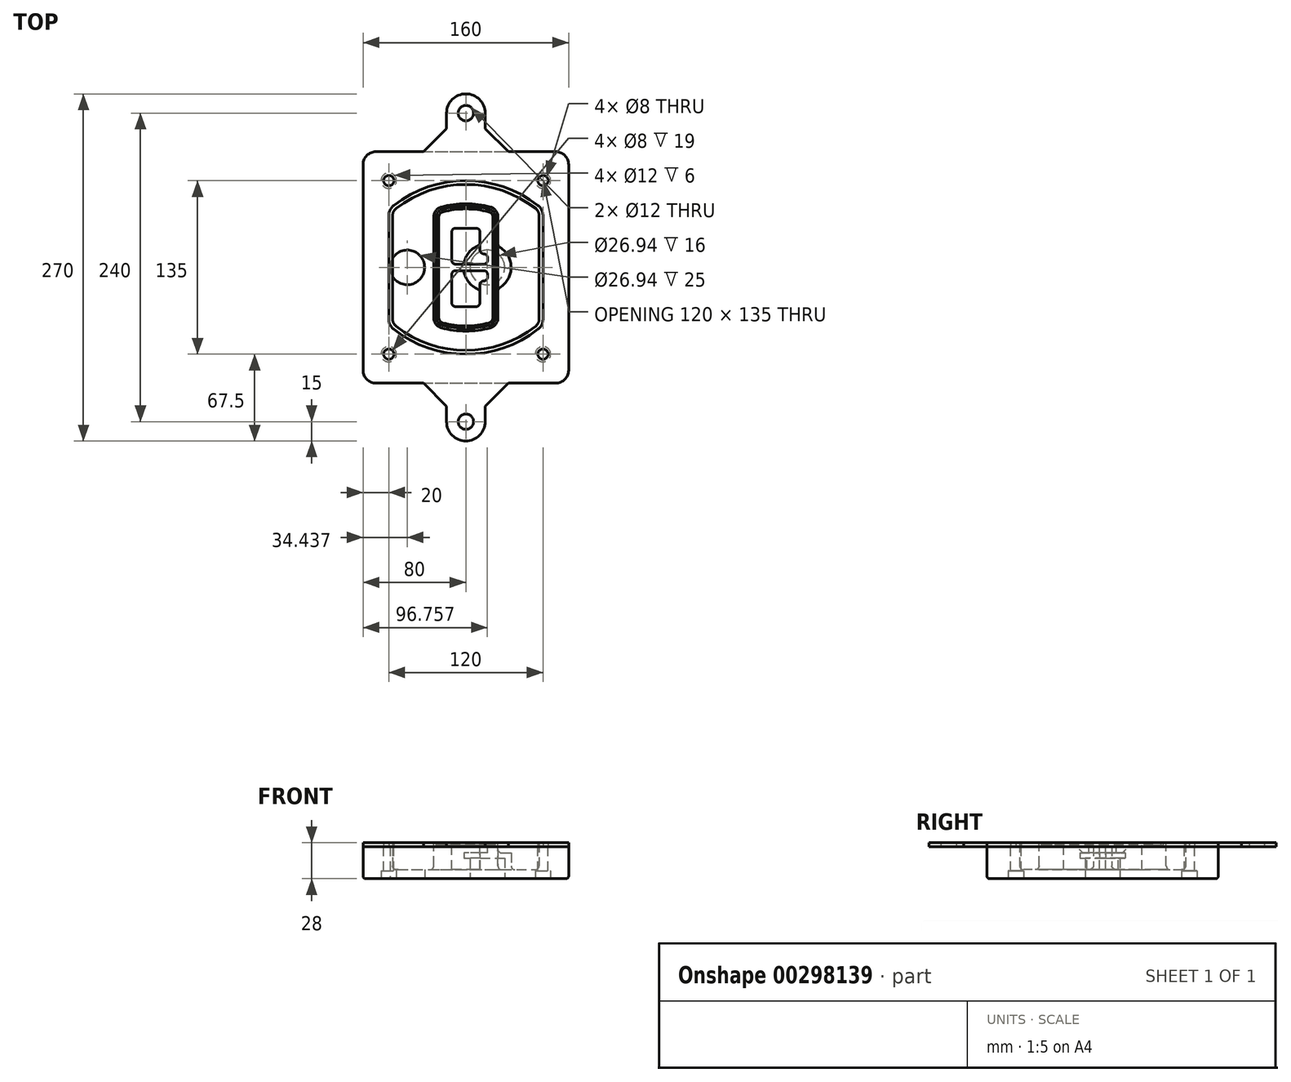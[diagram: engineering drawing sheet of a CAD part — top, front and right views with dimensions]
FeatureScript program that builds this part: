
annotation { "Feature Type Name" : "Feature", "Feature Type Description" : "" }
export const myFeature = defineFeature(function(context is Context, id is Id, definition is map)
    precondition{}
    {
        {
            var Q0;
            Q0=qCreatedBy(makeId("Top.planeOp"),FACE);
            var sketch = newSketch(context, id + "F0", { "sketchPlane" : qUnion([Q0])});
            skPoint(sketch, "E0.rect.middle", {"position": v(0, 0) * mm});
            skLineSegment(sketch, "E1.bottom", {"start": v(-70, -90) * mm, "end": v(70, -90) * mm});
            skLineSegment(sketch, "E1.top", {"start": v(-70, 90) * mm, "end": v(70, 90) * mm});
            skLineSegment(sketch, "E1.left", {"start": v(-80, -80) * mm, "end": v(-80, 80) * mm});
            skLineSegment(sketch, "E1.right", {"start": v(80, -80) * mm, "end": v(80, 80) * mm});
            skLineSegment(sketch, "E2", {"start": v(-80, 90) * mm, "end": v(80, -90) * mm, "construction": true});
            skLineSegment(sketch, "E3", {"start": v(80, 90) * mm, "end": v(-80, -90) * mm, "construction": true});
            skCircle(sketch, "E4", {"center": v(-60, 67.5) * mm, "radius": 4 * mm});
            skCircle(sketch, "E5", {"center": v(60, 67.5) * mm, "radius": 4 * mm});
            skCircle(sketch, "E6", {"center": v(60, -67.5) * mm, "radius": 4 * mm});
            skCircle(sketch, "E7", {"center": v(-60, -67.5) * mm, "radius": 4 * mm});
            skLineSegment(sketch, "E8", {"start": v(-60, 67.5) * mm, "end": v(60, 67.5) * mm, "construction": true});
            skLineSegment(sketch, "E9", {"start": v(60, 67.5) * mm, "end": v(60, -67.5) * mm, "construction": true});
            skLineSegment(sketch, "E10", {"start": v(60, -67.5) * mm, "end": v(-60, -67.5) * mm, "construction": true});
            skLineSegment(sketch, "E11", {"start": v(-60, -67.5) * mm, "end": v(-60, 67.5) * mm, "construction": true});
            skLineSegment(sketch, "E12", {"start": v(-60, 40.3) * mm, "end": v(-60, -40.3) * mm});
            skLineSegment(sketch, "E13", {"start": v(60, 40.3) * mm, "end": v(60, -40.3) * mm});
            skArc(sketch, "E14", {"start": v(56.15, 48.18) * mm, "mid": v(0, 67.5) * mm, "end": v(-56.15, 48.18) * mm});
            skArc(sketch, "E15", {"start": v(-56.15, -48.18) * mm, "mid": v(0, -67.5) * mm, "end": v(56.15, -48.18) * mm});
            skLineSegment(sketch, "E16", {"start": v(-60, 0) * mm, "end": v(60, 0) * mm, "construction": true});
            skPoint(sketch, "E17.visualSharp", {"position": v(-60, -45) * mm});
            skArc(sketch, "E17.filletArc", {"start": v(-60, -40.3) * mm, "mid": v(-58.99, -44.68) * mm, "end": v(-56.15, -48.18) * mm});
            skPoint(sketch, "E18.visualSharp", {"position": v(-60, 45) * mm});
            skArc(sketch, "E18.filletArc", {"start": v(-56.15, 48.18) * mm, "mid": v(-58.99, 44.68) * mm, "end": v(-60, 40.3) * mm});
            skPoint(sketch, "E19.visualSharp", {"position": v(60, 45) * mm});
            skArc(sketch, "E19.filletArc", {"start": v(60, 40.3) * mm, "mid": v(58.99, 44.68) * mm, "end": v(56.15, 48.18) * mm});
            skPoint(sketch, "E20.visualSharp", {"position": v(60, -45) * mm});
            skArc(sketch, "E20.filletArc", {"start": v(56.15, -48.18) * mm, "mid": v(58.99, -44.68) * mm, "end": v(60, -40.3) * mm});
            skPoint(sketch, "E21.visualSharp", {"position": v(-80, 90) * mm});
            skArc(sketch, "E21.filletArc", {"start": v(-70, 90) * mm, "mid": v(-77.07, 87.07) * mm, "end": v(-80, 80) * mm});
            skPoint(sketch, "E22.visualSharp", {"position": v(80, 90) * mm});
            skArc(sketch, "E22.filletArc", {"start": v(80, 80) * mm, "mid": v(77.07, 87.07) * mm, "end": v(70, 90) * mm});
            skPoint(sketch, "E23.visualSharp", {"position": v(80, -90) * mm});
            skArc(sketch, "E23.filletArc", {"start": v(70, -90) * mm, "mid": v(77.07, -87.07) * mm, "end": v(80, -80) * mm});
            skPoint(sketch, "E24.visualSharp", {"position": v(-80, -90) * mm});
            skArc(sketch, "E24.filletArc", {"start": v(-80, -80) * mm, "mid": v(-77.07, -87.07) * mm, "end": v(-70, -90) * mm});
            skArc(sketch, "E25.0", {"start": v(57, 40.3) * mm, "mid": v(56.3, 43.36) * mm, "end": v(54.3, 45.81) * mm});
            skLineSegment(sketch, "E25.1", {"start": v(57, 40.3) * mm, "end": v(57, -40.3) * mm});
            skArc(sketch, "E25.2", {"start": v(54.3, -45.81) * mm, "mid": v(56.3, -43.36) * mm, "end": v(57, -40.3) * mm});
            skArc(sketch, "E25.3", {"start": v(-54.3, -45.81) * mm, "mid": v(0, -64.5) * mm, "end": v(54.3, -45.81) * mm});
            skArc(sketch, "E25.4", {"start": v(-57, -40.3) * mm, "mid": v(-56.3, -43.36) * mm, "end": v(-54.3, -45.81) * mm});
            skArc(sketch, "E25.5", {"start": v(54.3, 45.81) * mm, "mid": v(0, 64.5) * mm, "end": v(-54.3, 45.81) * mm});
            skLineSegment(sketch, "E25.6", {"start": v(-57, 40.3) * mm, "end": v(-57, -40.3) * mm});
            skArc(sketch, "E25.7", {"start": v(-54.3, 45.81) * mm, "mid": v(-56.3, 43.36) * mm, "end": v(-57, 40.3) * mm});
            skArc(sketch, "E26.0", {"start": v(-58.62, 51.33) * mm, "mid": v(-62.58, 46.43) * mm, "end": v(-64, 40.3) * mm});
            skArc(sketch, "E26.1", {"start": v(58.62, 51.33) * mm, "mid": v(0, 71.5) * mm, "end": v(-58.62, 51.33) * mm});
            skArc(sketch, "E26.2", {"start": v(64, 40.3) * mm, "mid": v(62.58, 46.43) * mm, "end": v(58.62, 51.33) * mm});
            skLineSegment(sketch, "E26.3", {"start": v(64, 40.3) * mm, "end": v(64, -40.3) * mm});
            skArc(sketch, "E26.4", {"start": v(58.62, -51.33) * mm, "mid": v(62.58, -46.43) * mm, "end": v(64, -40.3) * mm});
            skLineSegment(sketch, "E26.5", {"start": v(-64, 40.3) * mm, "end": v(-64, -40.3) * mm});
            skArc(sketch, "E26.6", {"start": v(-58.62, -51.33) * mm, "mid": v(0, -71.5) * mm, "end": v(58.62, -51.33) * mm});
            skArc(sketch, "E26.7", {"start": v(-64, -40.3) * mm, "mid": v(-62.58, -46.43) * mm, "end": v(-58.62, -51.33) * mm});
            skSolve(sketch);
        }
        {
            var Q0;
            Q0=makeQuery(id+"F0.imprint","IMPRINT",FACE,{"disambiguationData":[TD([[makeQuery(id+"F0.imprint","IMPRINT",EDGE,{"derivedFrom":sQuery(id+"F0.wireOp",EDGE,"E1.bottom")}),1.0]])]});
            var Q1;
            Q1=makeQuery(id+"F0.imprint","IMPRINT",FACE,{"disambiguationData":[TD([[makeQuery(id+"F0.imprint","IMPRINT",EDGE,{"derivedFrom":sQuery(id+"F0.wireOp",EDGE,"E12")}),1.0]])]});
            var Q2;
            Q2=makeQuery(id+"F0.imprint","IMPRINT",FACE,{"disambiguationData":[TD([[makeQuery(id+"F0.imprint","IMPRINT",EDGE,{"derivedFrom":sQuery(id+"F0.wireOp",EDGE,"E25.0")}),1.0]])]});
            var Q3;
            Q3=makeQuery(id+"F0.imprint","IMPRINT",FACE,{"disambiguationData":[TD([[makeQuery(id+"F0.imprint","IMPRINT",EDGE,{"derivedFrom":sQuery(id+"F0.wireOp",EDGE,"E12")}),-1.0]])]});
            extrude(context, id + "F1", {"entities" : qUnion([Q0, Q1, Q2, Q3]), "oppositeDirection" : true, "depth" : 25 * mm});
        }
        {
            var Q0;
            Q0=makeQuery(id+"F0.imprint","IMPRINT",FACE,{"disambiguationData":[TD([[makeQuery(id+"F0.imprint","IMPRINT",EDGE,{"derivedFrom":sQuery(id+"F0.wireOp",EDGE,"E12")}),1.0]])]});
            extrude(context, id + "F2", {"entities" : qUnion([Q0]), "operationType" : NewBodyOperationType.ADD, "depth" : 3 * mm});
        }
        {
            var Q0;
            Q0=makeQuery(id+"F0.imprint","IMPRINT",FACE,{"disambiguationData":[TD([[makeQuery(id+"F0.imprint","IMPRINT",EDGE,{"derivedFrom":sQuery(id+"F0.wireOp",EDGE,"E25.0")}),1.0]])]});
            extrude(context, id + "F3", {"entities" : qUnion([Q0]), "operationType" : NewBodyOperationType.REMOVE, "oppositeDirection" : true, "depth" : 18 * mm});
        }
        {
            var Q0;
            Q0=makeQuery(id+"F2.opExtrude","CAP_FACE",FACE,{"disambiguationData":[OSD([sQuery(id+"F0.wireOp",EDGE,"E12"),sQuery(id+"F0.wireOp",EDGE,"E13"),sQuery(id+"F0.wireOp",EDGE,"E14"),sQuery(id+"F0.wireOp",EDGE,"E15"),sQuery(id+"F0.wireOp",EDGE,"E17.filletArc"),sQuery(id+"F0.wireOp",EDGE,"E18.filletArc"),sQuery(id+"F0.wireOp",EDGE,"E19.filletArc"),sQuery(id+"F0.wireOp",EDGE,"E20.filletArc"),sQuery(id+"F0.wireOp",EDGE,"E25.0"),sQuery(id+"F0.wireOp",EDGE,"E25.1"),sQuery(id+"F0.wireOp",EDGE,"E25.2"),sQuery(id+"F0.wireOp",EDGE,"E25.3"),sQuery(id+"F0.wireOp",EDGE,"E25.4"),sQuery(id+"F0.wireOp",EDGE,"E25.5"),sQuery(id+"F0.wireOp",EDGE,"E25.6"),sQuery(id+"F0.wireOp",EDGE,"E25.7")])],"isStart":false});
            var sketch = newSketch(context, id + "F4", { "sketchPlane" : qUnion([Q0])});
            skArc(sketch, "E27.0", {"start": v(-19.08, -46.97) * mm, "mid": v(0, -49.5) * mm, "end": v(19.08, -46.97) * mm});
            skArc(sketch, "E28.0", {"start": v(19.08, 46.97) * mm, "mid": v(0, 49.5) * mm, "end": v(-19.08, 46.97) * mm});
            skLineSegment(sketch, "E29", {"start": v(-25, 39.25) * mm, "end": v(-25, -39.25) * mm});
            skLineSegment(sketch, "E30", {"start": v(25, 39.25) * mm, "end": v(25, -39.25) * mm});
            skLineSegment(sketch, "E31", {"start": v(-25, 45.1) * mm, "end": v(25, 45.1) * mm, "construction": true});
            skLineSegment(sketch, "E32", {"start": v(-25, -45.1) * mm, "end": v(25, -45.1) * mm, "construction": true});
            skPoint(sketch, "E33.visualSharp", {"position": v(-25, 45.1) * mm});
            skArc(sketch, "E33.filletArc", {"start": v(-19.08, 46.97) * mm, "mid": v(-23.35, 44.11) * mm, "end": v(-25, 39.25) * mm});
            skPoint(sketch, "E34.visualSharp", {"position": v(25, 45.1) * mm});
            skArc(sketch, "E34.filletArc", {"start": v(25, 39.25) * mm, "mid": v(23.35, 44.11) * mm, "end": v(19.08, 46.97) * mm});
            skPoint(sketch, "E35.visualSharp", {"position": v(25, -45.1) * mm});
            skArc(sketch, "E35.filletArc", {"start": v(19.08, -46.97) * mm, "mid": v(23.35, -44.11) * mm, "end": v(25, -39.25) * mm});
            skPoint(sketch, "E36.visualSharp", {"position": v(-25, -45.1) * mm});
            skArc(sketch, "E36.filletArc", {"start": v(-25, -39.25) * mm, "mid": v(-23.35, -44.11) * mm, "end": v(-19.08, -46.97) * mm});
            skArc(sketch, "E37.0", {"start": v(54.3, 45.81) * mm, "mid": v(0, 64.5) * mm, "end": v(-54.3, 45.81) * mm});
            skArc(sketch, "E37.1", {"start": v(-54.3, 45.81) * mm, "mid": v(-56.3, 43.36) * mm, "end": v(-57, 40.3) * mm});
            skLineSegment(sketch, "E37.2", {"start": v(-57, 40.3) * mm, "end": v(-57, -40.3) * mm});
            skArc(sketch, "E37.3", {"start": v(-57, -40.3) * mm, "mid": v(-56.3, -43.36) * mm, "end": v(-54.3, -45.81) * mm});
            skArc(sketch, "E37.4", {"start": v(-54.3, -45.81) * mm, "mid": v(0, -64.5) * mm, "end": v(54.3, -45.81) * mm});
            skArc(sketch, "E37.5", {"start": v(54.3, -45.81) * mm, "mid": v(56.3, -43.36) * mm, "end": v(57, -40.3) * mm});
            skLineSegment(sketch, "E37.6", {"start": v(57, 40.3) * mm, "end": v(57, -40.3) * mm});
            skArc(sketch, "E37.7", {"start": v(57, 40.3) * mm, "mid": v(56.3, 43.36) * mm, "end": v(54.3, 45.81) * mm});
            skLineSegment(sketch, "E38.0", {"start": v(23, 39.25) * mm, "end": v(23, -39.25) * mm});
            skArc(sketch, "E38.1", {"start": v(18.56, -45.04) * mm, "mid": v(21.76, -42.9) * mm, "end": v(23, -39.25) * mm});
            skArc(sketch, "E38.2", {"start": v(-18.56, -45.04) * mm, "mid": v(0, -47.5) * mm, "end": v(18.56, -45.04) * mm});
            skArc(sketch, "E38.3", {"start": v(-23, -39.25) * mm, "mid": v(-21.76, -42.9) * mm, "end": v(-18.56, -45.04) * mm});
            skLineSegment(sketch, "E38.4", {"start": v(-23, 39.25) * mm, "end": v(-23, -39.25) * mm});
            skArc(sketch, "E38.5", {"start": v(23, 39.25) * mm, "mid": v(21.76, 42.9) * mm, "end": v(18.56, 45.04) * mm});
            skArc(sketch, "E38.6", {"start": v(-18.56, 45.04) * mm, "mid": v(-21.76, 42.9) * mm, "end": v(-23, 39.25) * mm});
            skArc(sketch, "E38.7", {"start": v(18.56, 45.04) * mm, "mid": v(0, 47.5) * mm, "end": v(-18.56, 45.04) * mm});
            skArc(sketch, "E39.0", {"start": v(21, 39.25) * mm, "mid": v(20.18, 41.68) * mm, "end": v(18.04, 43.1) * mm});
            skLineSegment(sketch, "E39.1", {"start": v(21, 39.25) * mm, "end": v(21, -39.25) * mm});
            skArc(sketch, "E39.2", {"start": v(18.04, -43.1) * mm, "mid": v(20.18, -41.68) * mm, "end": v(21, -39.25) * mm});
            skArc(sketch, "E39.3", {"start": v(-18.04, -43.1) * mm, "mid": v(0, -45.5) * mm, "end": v(18.04, -43.1) * mm});
            skArc(sketch, "E39.4", {"start": v(-21, -39.25) * mm, "mid": v(-20.18, -41.68) * mm, "end": v(-18.04, -43.1) * mm});
            skArc(sketch, "E39.5", {"start": v(18.04, 43.1) * mm, "mid": v(0, 45.5) * mm, "end": v(-18.04, 43.1) * mm});
            skLineSegment(sketch, "E39.6", {"start": v(-21, 39.25) * mm, "end": v(-21, -39.25) * mm});
            skArc(sketch, "E39.7", {"start": v(-18.04, 43.1) * mm, "mid": v(-20.18, 41.68) * mm, "end": v(-21, 39.25) * mm});
            skLineSegment(sketch, "E40", {"start": v(-25, 0) * mm, "end": v(25, 0) * mm, "construction": true});
            skLineSegment(sketch, "E41", {"start": v(-11, 5.5) * mm, "end": v(-11, 27.5) * mm});
            skLineSegment(sketch, "E42", {"start": v(-8, 30.5) * mm, "end": v(8, 30.5) * mm});
            skLineSegment(sketch, "E43", {"start": v(11, 27.5) * mm, "end": v(11, 13.5) * mm});
            skLineSegment(sketch, "E44", {"start": v(14, 10.5) * mm, "end": v(14, 10.5) * mm});
            skLineSegment(sketch, "E45", {"start": v(17, 7.5) * mm, "end": v(17, 5.5) * mm});
            skLineSegment(sketch, "E46", {"start": v(14, 2.5) * mm, "end": v(-8, 2.5) * mm});
            skPoint(sketch, "E47.visualSharp", {"position": v(-11, 30.5) * mm});
            skArc(sketch, "E47.filletArc", {"start": v(-8, 30.5) * mm, "mid": v(-10.12, 29.62) * mm, "end": v(-11, 27.5) * mm});
            skPoint(sketch, "E48.visualSharp", {"position": v(11, 30.5) * mm});
            skArc(sketch, "E48.filletArc", {"start": v(11, 27.5) * mm, "mid": v(10.12, 29.62) * mm, "end": v(8, 30.5) * mm});
            skPoint(sketch, "E49.visualSharp", {"position": v(11, 10.5) * mm});
            skArc(sketch, "E49.filletArc", {"start": v(11, 13.5) * mm, "mid": v(11.88, 11.38) * mm, "end": v(14, 10.5) * mm});
            skPoint(sketch, "E50.visualSharp", {"position": v(17, 10.5) * mm});
            skArc(sketch, "E50.filletArc", {"start": v(17, 7.5) * mm, "mid": v(16.12, 9.62) * mm, "end": v(14, 10.5) * mm});
            skPoint(sketch, "E51.visualSharp", {"position": v(17, 2.5) * mm});
            skArc(sketch, "E51.filletArc", {"start": v(14, 2.5) * mm, "mid": v(16.12, 3.38) * mm, "end": v(17, 5.5) * mm});
            skPoint(sketch, "E52.visualSharp", {"position": v(-11, 2.5) * mm});
            skArc(sketch, "E52.filletArc", {"start": v(-11, 5.5) * mm, "mid": v(-10.12, 3.38) * mm, "end": v(-8, 2.5) * mm});
            skLineSegment(sketch, "E53.0.MirrorCS", {"start": v(14, -2.5) * mm, "end": v(-8, -2.5) * mm});
            skArc(sketch, "E54.0.MirrorCS", {"start": v(-11, -5.5) * mm, "mid": v(-10.12, -3.38) * mm, "end": v(-8, -2.5) * mm});
            skLineSegment(sketch, "E55.0.MirrorCS", {"start": v(-11, -5.5) * mm, "end": v(-11, -27.5) * mm});
            skArc(sketch, "E56.0.MirrorCS", {"start": v(-8, -30.5) * mm, "mid": v(-10.12, -29.62) * mm, "end": v(-11, -27.5) * mm});
            skLineSegment(sketch, "E57.0.MirrorCS", {"start": v(-8, -30.5) * mm, "end": v(8, -30.5) * mm});
            skArc(sketch, "E58.0.MirrorCS", {"start": v(11, -27.5) * mm, "mid": v(10.12, -29.62) * mm, "end": v(8, -30.5) * mm});
            skLineSegment(sketch, "E59.0.MirrorCS", {"start": v(11, -27.5) * mm, "end": v(11, -13.5) * mm});
            skArc(sketch, "E60.0.MirrorCS", {"start": v(11, -13.5) * mm, "mid": v(11.88, -11.38) * mm, "end": v(14, -10.5) * mm});
            skArc(sketch, "E61.0.MirrorCS", {"start": v(17, -7.5) * mm, "mid": v(16.12, -9.62) * mm, "end": v(14, -10.5) * mm});
            skLineSegment(sketch, "E62.0.MirrorCS", {"start": v(17, -7.5) * mm, "end": v(17, -5.5) * mm});
            skArc(sketch, "E63.0.MirrorCS", {"start": v(14, -2.5) * mm, "mid": v(16.12, -3.38) * mm, "end": v(17, -5.5) * mm});
            skSolve(sketch);
        }
        {
            var Q0;
            Q0=makeQuery(id+"F4.imprint","IMPRINT",FACE,{"disambiguationData":[TD([[makeQuery(id+"F4.imprint","IMPRINT",EDGE,{"derivedFrom":sQuery(id+"F4.wireOp",EDGE,"E27.0")}),1.0]])]});
            var Q1;
            Q1=makeQuery(id+"F4.imprint","IMPRINT",FACE,{"disambiguationData":[TD([[makeQuery(id+"F4.imprint","IMPRINT",EDGE,{"derivedFrom":sQuery(id+"F4.wireOp",EDGE,"E38.0")}),-1.0]])]});
            var Q2;
            Q2=makeQuery(id+"F4.imprint","IMPRINT",FACE,{"disambiguationData":[TD([[makeQuery(id+"F4.imprint","IMPRINT",EDGE,{"derivedFrom":sQuery(id+"F4.wireOp",EDGE,"E39.0")}),1.0]])]});
            extrude(context, id + "F5", {"entities" : qUnion([Q0, Q1, Q2]), "operationType" : NewBodyOperationType.ADD, "endBound" : BoundingType.UP_TO_NEXT, "oppositeDirection" : true, "depth" : 25 * mm});
        }
        {
            var Q0;
            Q0=makeQuery(id+"F4.imprint","IMPRINT",FACE,{"disambiguationData":[TD([[makeQuery(id+"F4.imprint","IMPRINT",EDGE,{"derivedFrom":sQuery(id+"F4.wireOp",EDGE,"E38.0")}),-1.0]])]});
            extrude(context, id + "F6", {"entities" : qUnion([Q0]), "operationType" : NewBodyOperationType.REMOVE, "oppositeDirection" : true, "depth" : 2 * mm});
        }
        {
            var Q0;
            Q0=makeQuery(id+"F1.opExtrude","CAP_FACE",FACE,{"disambiguationData":[OSD([sQuery(id+"F0.wireOp",EDGE,"E1.bottom"),sQuery(id+"F0.wireOp",EDGE,"E1.top"),sQuery(id+"F0.wireOp",EDGE,"E1.left"),sQuery(id+"F0.wireOp",EDGE,"E1.right"),sQuery(id+"F0.wireOp",EDGE,"E4"),sQuery(id+"F0.wireOp",EDGE,"E5"),sQuery(id+"F0.wireOp",EDGE,"E6"),sQuery(id+"F0.wireOp",EDGE,"E7"),sQuery(id+"F0.wireOp",EDGE,"E21.filletArc"),sQuery(id+"F0.wireOp",EDGE,"E22.filletArc"),sQuery(id+"F0.wireOp",EDGE,"E23.filletArc"),sQuery(id+"F0.wireOp",EDGE,"E24.filletArc")])],"isStart":false});
            var sketch = newSketch(context, id + "F7", { "sketchPlane" : qUnion([Q0])});
            skCircle(sketch, "E64", {"center": v(16.76, 0) * mm, "radius": 13.47 * mm});
            skCircle(sketch, "E65", {"center": v(-45.56, 0) * mm, "radius": 13.47 * mm});
            skLineSegment(sketch, "E66", {"start": v(80, 0) * mm, "end": v(-80, 0) * mm});
            skCircle(sketch, "E67", {"center": v(16.76, 0) * mm, "radius": 18.47 * mm});
            skCircle(sketch, "E68", {"center": v(60, -67.5) * mm, "radius": 6 * mm});
            skCircle(sketch, "E69", {"center": v(-60, -67.5) * mm, "radius": 6 * mm});
            skCircle(sketch, "E70", {"center": v(-60, 67.5) * mm, "radius": 6 * mm});
            skCircle(sketch, "E71", {"center": v(60, 67.5) * mm, "radius": 6 * mm});
            skSolve(sketch);
        }
        {
            var Q0;
            {var subQ1=sQuery(id+"F7.wireOp",EDGE,"E66");var subQ4=sQuery(id+"F7.wireOp",EDGE,"E64");var subQ6=makeQuery(id+"F7.imprint","INTERSECT",VERTEX,{"disambiguationData":[OD(0.0)],"derivedFrom":[subQ4,subQ1]});Q0=makeQuery(id+"F7.imprint","IMPRINT",FACE,{"disambiguationData":[TD([[makeQuery(id+"F7.imprint","IMPRINT",EDGE,{"disambiguationData":[TD([[subQ6,-1.0]])],"derivedFrom":subQ4}),-1.0]])]});}
            var Q1;
            {var subQ0=sQuery(id+"F7.wireOp",EDGE,"E66");var subQ1=sQuery(id+"F7.wireOp",EDGE,"E64");var subQ3=makeQuery(id+"F7.imprint","INTERSECT",VERTEX,{"disambiguationData":[OD(0.0)],"derivedFrom":[subQ1,subQ0]});Q1=makeQuery(id+"F7.imprint","IMPRINT",FACE,{"disambiguationData":[TD([[makeQuery(id+"F7.imprint","IMPRINT",EDGE,{"disambiguationData":[TD([[subQ3,-1.0]])],"derivedFrom":subQ1}),1.0]])]});}
            var Q2;
            {var subQ0=sQuery(id+"F7.wireOp",EDGE,"E66");var subQ1=sQuery(id+"F7.wireOp",EDGE,"E64");var subQ3=makeQuery(id+"F7.imprint","INTERSECT",VERTEX,{"disambiguationData":[OD(0.0)],"derivedFrom":[subQ1,subQ0]});Q2=makeQuery(id+"F7.imprint","IMPRINT",FACE,{"disambiguationData":[TD([[makeQuery(id+"F7.imprint","IMPRINT",EDGE,{"disambiguationData":[TD([[subQ3,1.0]])],"derivedFrom":subQ1}),1.0]])]});}
            var Q3;
            {var subQ1=sQuery(id+"F7.wireOp",EDGE,"E66");var subQ4=sQuery(id+"F7.wireOp",EDGE,"E64");var subQ6=makeQuery(id+"F7.imprint","INTERSECT",VERTEX,{"disambiguationData":[OD(0.0)],"derivedFrom":[subQ4,subQ1]});Q3=makeQuery(id+"F7.imprint","IMPRINT",FACE,{"disambiguationData":[TD([[makeQuery(id+"F7.imprint","IMPRINT",EDGE,{"disambiguationData":[TD([[subQ6,1.0]])],"derivedFrom":subQ4}),-1.0]])]});}
            extrude(context, id + "F8", {"entities" : qUnion([Q0, Q1, Q2, Q3]), "operationType" : NewBodyOperationType.ADD, "oppositeDirection" : true, "depth" : 20 * mm});
        }
        {
            var Q0;
            {var subQ0=sQuery(id+"F7.wireOp",EDGE,"E66");var subQ1=sQuery(id+"F7.wireOp",EDGE,"E64");var subQ3=makeQuery(id+"F7.imprint","INTERSECT",VERTEX,{"disambiguationData":[OD(0.0)],"derivedFrom":[subQ1,subQ0]});Q0=makeQuery(id+"F7.imprint","IMPRINT",FACE,{"disambiguationData":[TD([[makeQuery(id+"F7.imprint","IMPRINT",EDGE,{"disambiguationData":[TD([[subQ3,-1.0]])],"derivedFrom":subQ1}),1.0]])]});}
            var Q1;
            {var subQ0=sQuery(id+"F7.wireOp",EDGE,"E66");var subQ1=sQuery(id+"F7.wireOp",EDGE,"E64");var subQ3=makeQuery(id+"F7.imprint","INTERSECT",VERTEX,{"disambiguationData":[OD(0.0)],"derivedFrom":[subQ1,subQ0]});Q1=makeQuery(id+"F7.imprint","IMPRINT",FACE,{"disambiguationData":[TD([[makeQuery(id+"F7.imprint","IMPRINT",EDGE,{"disambiguationData":[TD([[subQ3,1.0]])],"derivedFrom":subQ1}),1.0]])]});}
            extrude(context, id + "F9", {"entities" : qUnion([Q0, Q1]), "operationType" : NewBodyOperationType.REMOVE, "oppositeDirection" : true, "depth" : 16 * mm});
        }
        {
            var Q0;
            {var subQ0=sQuery(id+"F7.wireOp",EDGE,"E66");var subQ1=sQuery(id+"F7.wireOp",EDGE,"E65");var subQ3=makeQuery(id+"F7.imprint","INTERSECT",VERTEX,{"disambiguationData":[OD(0.0)],"derivedFrom":[subQ1,subQ0]});Q0=makeQuery(id+"F7.imprint","IMPRINT",FACE,{"disambiguationData":[TD([[makeQuery(id+"F7.imprint","IMPRINT",EDGE,{"disambiguationData":[TD([[subQ3,-1.0]])],"derivedFrom":subQ1}),1.0]])]});}
            var Q1;
            {var subQ0=sQuery(id+"F7.wireOp",EDGE,"E66");var subQ1=sQuery(id+"F7.wireOp",EDGE,"E65");var subQ3=makeQuery(id+"F7.imprint","INTERSECT",VERTEX,{"disambiguationData":[OD(0.0)],"derivedFrom":[subQ1,subQ0]});Q1=makeQuery(id+"F7.imprint","IMPRINT",FACE,{"disambiguationData":[TD([[makeQuery(id+"F7.imprint","IMPRINT",EDGE,{"disambiguationData":[TD([[subQ3,1.0]])],"derivedFrom":subQ1}),1.0]])]});}
            extrude(context, id + "F10", {"entities" : qUnion([Q0, Q1]), "operationType" : NewBodyOperationType.REMOVE, "oppositeDirection" : true, "depth" : 25 * mm});
        }
        {
            var Q0;
            Q0=makeQuery(id+"F7.imprint","IMPRINT",FACE,{"disambiguationData":[TD([[makeQuery(id+"F7.imprint","IMPRINT",EDGE,{"derivedFrom":sQuery(id+"F7.wireOp",EDGE,"E68")}),1.0]])]});
            var Q1;
            Q1=makeQuery(id+"F7.imprint","IMPRINT",FACE,{"disambiguationData":[TD([[makeQuery(id+"F7.imprint","IMPRINT",EDGE,{"derivedFrom":makeQuery(id+"F1.opExtrude","CAP_EDGE",EDGE,{"disambiguationData":[OSD([sQuery(id+"F0.wireOp",EDGE,"E5")])],"isStart":false})}),-1.0]])]});
            var Q2;
            Q2=makeQuery(id+"F7.imprint","IMPRINT",FACE,{"disambiguationData":[TD([[makeQuery(id+"F7.imprint","IMPRINT",EDGE,{"derivedFrom":sQuery(id+"F7.wireOp",EDGE,"E69")}),1.0]])]});
            var Q3;
            Q3=makeQuery(id+"F7.imprint","IMPRINT",FACE,{"disambiguationData":[TD([[makeQuery(id+"F7.imprint","IMPRINT",EDGE,{"derivedFrom":makeQuery(id+"F1.opExtrude","CAP_EDGE",EDGE,{"disambiguationData":[OSD([sQuery(id+"F0.wireOp",EDGE,"E4")])],"isStart":false})}),-1.0]])]});
            var Q4;
            Q4=makeQuery(id+"F7.imprint","IMPRINT",FACE,{"disambiguationData":[TD([[makeQuery(id+"F7.imprint","IMPRINT",EDGE,{"derivedFrom":sQuery(id+"F7.wireOp",EDGE,"E70")}),1.0]])]});
            var Q5;
            Q5=makeQuery(id+"F7.imprint","IMPRINT",FACE,{"disambiguationData":[TD([[makeQuery(id+"F7.imprint","IMPRINT",EDGE,{"derivedFrom":makeQuery(id+"F1.opExtrude","CAP_EDGE",EDGE,{"disambiguationData":[OSD([sQuery(id+"F0.wireOp",EDGE,"E7")])],"isStart":false})}),-1.0]])]});
            var Q6;
            Q6=makeQuery(id+"F7.imprint","IMPRINT",FACE,{"disambiguationData":[TD([[makeQuery(id+"F7.imprint","IMPRINT",EDGE,{"derivedFrom":sQuery(id+"F7.wireOp",EDGE,"E71")}),1.0]])]});
            var Q7;
            Q7=makeQuery(id+"F7.imprint","IMPRINT",FACE,{"disambiguationData":[TD([[makeQuery(id+"F7.imprint","IMPRINT",EDGE,{"derivedFrom":makeQuery(id+"F1.opExtrude","CAP_EDGE",EDGE,{"disambiguationData":[OSD([sQuery(id+"F0.wireOp",EDGE,"E6")])],"isStart":false})}),-1.0]])]});
            extrude(context, id + "F11", {"entities" : qUnion([Q0, Q1, Q2, Q3, Q4, Q5, Q6, Q7]), "operationType" : NewBodyOperationType.REMOVE, "oppositeDirection" : true, "depth" : 6 * mm});
        }
        {
            var Q0;
            Q0=makeQuery(id+"F9.boolean.opBoolean","COPY",FACE,{"derivedFrom":makeQuery(id+"F9.opExtrude","CAP_FACE",FACE,{"disambiguationData":[OSD([sQuery(id+"F7.wireOp",EDGE,"E64")])],"isStart":false})});
            var sketch = newSketch(context, id + "F12", { "sketchPlane" : qUnion([Q0])});
            skArc(sketch, "E72.0", {"start": v(11, 17.55) * mm, "mid": v(2.57, 11.82) * mm, "end": v(-1.54, 2.5) * mm});
            skArc(sketch, "E72.1", {"start": v(-1.54, -2.5) * mm, "mid": v(2.57, -11.82) * mm, "end": v(11, -17.55) * mm});
            skLineSegment(sketch, "E73", {"start": v(-1.54, -2.5) * mm, "end": v(14, -2.5) * mm});
            skLineSegment(sketch, "E74.0", {"start": v(14, 2.5) * mm, "end": v(-1.54, 2.5) * mm});
            skArc(sketch, "E74.1", {"start": v(14, 2.5) * mm, "mid": v(16.12, 3.38) * mm, "end": v(17, 5.5) * mm});
            skLineSegment(sketch, "E74.2", {"start": v(17, 7.5) * mm, "end": v(17, 5.5) * mm});
            skArc(sketch, "E74.3", {"start": v(17, 7.5) * mm, "mid": v(16.12, 9.62) * mm, "end": v(14, 10.5) * mm});
            skArc(sketch, "E74.4", {"start": v(11, 13.5) * mm, "mid": v(11.88, 11.38) * mm, "end": v(14, 10.5) * mm});
            skLineSegment(sketch, "E74.5", {"start": v(11, 17.55) * mm, "end": v(11, 13.5) * mm});
            skLineSegment(sketch, "E74.7", {"start": v(14, -2.5) * mm, "end": v(-1.54, -2.5) * mm});
            skArc(sketch, "E74.8", {"start": v(14, -2.5) * mm, "mid": v(16.12, -3.38) * mm, "end": v(17, -5.5) * mm});
            skLineSegment(sketch, "E74.9", {"start": v(17, -7.5) * mm, "end": v(17, -5.5) * mm});
            skArc(sketch, "E74.10", {"start": v(17, -7.5) * mm, "mid": v(16.12, -9.62) * mm, "end": v(14, -10.5) * mm});
            skArc(sketch, "E74.11", {"start": v(11, -13.5) * mm, "mid": v(11.88, -11.38) * mm, "end": v(14, -10.5) * mm});
            skLineSegment(sketch, "E74.12", {"start": v(11, -17.55) * mm, "end": v(11, -13.5) * mm});
            skPoint(sketch, "E75.orphan", {"position": v(11, -27.5) * mm});
            skPoint(sketch, "E76.orphan", {"position": v(-8, -2.5) * mm});
            skPoint(sketch, "E77.orphan", {"position": v(-8, 2.5) * mm});
            skPoint(sketch, "E78.orphan", {"position": v(11, 27.5) * mm});
            skSolve(sketch);
        }
        {
            var Q0;
            {var subQ7=sQuery(id+"F12.wireOp",EDGE,"E72.0");var subQ14=sQuery(id+"F12.wireOp",EDGE,"E72.1");var subQ16=sQuery(id+"F12.wireOp",EDGE,"E74.1");var subQ18=sQuery(id+"F12.wireOp",EDGE,"E74.8");Q0=qUnion([makeQuery(id+"F12.imprint","IMPRINT",FACE,{"disambiguationData":[TD([[makeQuery(id+"F12.imprint","IMPRINT",EDGE,{"derivedFrom":subQ7}),1.0]])]}),makeQuery(id+"F12.imprint","IMPRINT",FACE,{"disambiguationData":[TD([[makeQuery(id+"F12.imprint","IMPRINT",EDGE,{"derivedFrom":subQ14}),1.0]])]}),makeQuery(id+"F12.imprint","IMPRINT",FACE,{"disambiguationData":[TD([[makeQuery(id+"F12.imprint","IMPRINT",EDGE,{"derivedFrom":subQ16}),1.0]])]}),makeQuery(id+"F12.imprint","IMPRINT",FACE,{"disambiguationData":[TD([[makeQuery(id+"F12.imprint","IMPRINT",EDGE,{"derivedFrom":subQ18}),-1.0]])]})]);}
            var Q1;
            Q1=makeQuery(id+"F5.boolean.opBoolean","SPLIT",FACE,{"disambiguationData":[TD([makeQuery(id+"F5.opExtrude","SWEPT_FACE",FACE,{"disambiguationData":[OSD([sQuery(id+"F4.wireOp",EDGE,"E41")])]})])],"derivedFrom":makeQuery(id+"F3.boolean.opBoolean","COPY",FACE,{"derivedFrom":makeQuery(id+"F3.opExtrude","CAP_FACE",FACE,{"disambiguationData":[OSD([sQuery(id+"F0.wireOp",EDGE,"E25.0"),sQuery(id+"F0.wireOp",EDGE,"E25.1"),sQuery(id+"F0.wireOp",EDGE,"E25.2"),sQuery(id+"F0.wireOp",EDGE,"E25.3"),sQuery(id+"F0.wireOp",EDGE,"E25.4"),sQuery(id+"F0.wireOp",EDGE,"E25.5"),sQuery(id+"F0.wireOp",EDGE,"E25.6"),sQuery(id+"F0.wireOp",EDGE,"E25.7")])],"isStart":false})})});
            extrude(context, id + "F13", {"entities" : qUnion([Q0]), "operationType" : NewBodyOperationType.REMOVE, "endBound" : BoundingType.UP_TO_SURFACE, "endBoundEntityFace" : qUnion([Q1]), "depth" : 25 * mm});
        }
        {
            var Q0;
            Q0=makeQuery(id+"F3.boolean.opBoolean","COPY",EDGE,{"derivedFrom":makeQuery(id+"F3.opExtrude","CAP_EDGE",EDGE,{"disambiguationData":[OSD([sQuery(id+"F0.wireOp",EDGE,"E25.6")])],"isStart":false})});
            var Q1;
            Q1=makeQuery(id+"F8.boolean.opBoolean","INTERSECT",EDGE,{"derivedFrom":[makeQuery(id+"F5.opExtrude","SWEPT_FACE",FACE,{"disambiguationData":[OSD([sQuery(id+"F4.wireOp",EDGE,"E30")])]}),makeQuery(id+"F8.opExtrude","CAP_FACE",FACE,{"disambiguationData":[OSD([sQuery(id+"F7.wireOp",EDGE,"E67")])],"isStart":false})]});
            var Q2;
            Q2=makeQuery(id+"F8.boolean.opBoolean","INTERSECT",EDGE,{"disambiguationData":[OD(1.0)],"derivedFrom":[makeQuery(id+"F5.opExtrude","SWEPT_FACE",FACE,{"disambiguationData":[OSD([sQuery(id+"F4.wireOp",EDGE,"E30")])]}),makeQuery(id+"F8.opExtrude","SWEPT_FACE",FACE,{"disambiguationData":[OSD([sQuery(id+"F7.wireOp",EDGE,"E67")])]})]});
            var Q3;
            {var subQ0=sQuery(id+"F4.wireOp",EDGE,"E30");Q3=makeQuery(id+"F8.boolean.opBoolean","SPLIT",EDGE,{"disambiguationData":[TD([makeQuery(id+"F5.opExtrude","SWEPT_FACE",FACE,{"disambiguationData":[OSD([sQuery(id+"F4.wireOp",EDGE,"E35.filletArc")])]})])],"derivedFrom":makeQuery(id+"F5.opExtrude","CAP_EDGE",EDGE,{"disambiguationData":[OSD([subQ0])],"isStart":false})});}
            var Q4;
            {var subQ0=sQuery(id+"F0.wireOp",EDGE,"E25.7");var subQ1=sQuery(id+"F0.wireOp",EDGE,"E25.1");var subQ2=sQuery(id+"F0.wireOp",EDGE,"E25.6");var subQ3=sQuery(id+"F0.wireOp",EDGE,"E25.5");var subQ4=sQuery(id+"F0.wireOp",EDGE,"E25.4");var subQ5=sQuery(id+"F0.wireOp",EDGE,"E25.0");var subQ6=sQuery(id+"F0.wireOp",EDGE,"E25.2");var subQ7=sQuery(id+"F0.wireOp",EDGE,"E25.3");Q4=makeQuery(id+"F8.boolean.opBoolean","INTERSECT",EDGE,{"derivedFrom":[makeQuery(id+"F5.boolean.opBoolean","SPLIT",FACE,{"disambiguationData":[TD([makeQuery(id+"F2.opExtrude","SWEPT_FACE",FACE,{"disambiguationData":[OSD([subQ5])]})])],"derivedFrom":makeQuery(id+"F3.boolean.opBoolean","COPY",FACE,{"derivedFrom":makeQuery(id+"F3.opExtrude","CAP_FACE",FACE,{"disambiguationData":[OSD([subQ5,subQ1,subQ6,subQ7,subQ4,subQ3,subQ2,subQ0])],"isStart":false})})}),makeQuery(id+"F8.opExtrude","SWEPT_FACE",FACE,{"disambiguationData":[OSD([sQuery(id+"F7.wireOp",EDGE,"E67")])]})]});}
            var Q5;
            Q5=makeQuery(id+"F8.boolean.opBoolean","INTERSECT",EDGE,{"disambiguationData":[OD(0.0)],"derivedFrom":[makeQuery(id+"F5.opExtrude","SWEPT_FACE",FACE,{"disambiguationData":[OSD([sQuery(id+"F4.wireOp",EDGE,"E30")])]}),makeQuery(id+"F8.opExtrude","SWEPT_FACE",FACE,{"disambiguationData":[OSD([sQuery(id+"F7.wireOp",EDGE,"E67")])]})]});
            fillet(context, id + "F14", {"entities" : qUnion([Q0, Q1, Q2, Q3, Q4, Q5]), "radius" : 3 * mm, "tangentPropagation" : true, "allowEdgeOverflow" : false});
        }
        {
            var Q0;
            Q0=makeQuery(id+"F1.opExtrude","CAP_EDGE",EDGE,{"disambiguationData":[OSD([sQuery(id+"F0.wireOp",EDGE,"E1.bottom")])],"isStart":false});
            fillet(context, id + "F15", {"entities" : qUnion([Q0]), "radius" : 2 * mm, "tangentPropagation" : true, "allowEdgeOverflow" : false});
        }
        {
            var Q0;
            {var subQ0=sQuery(id+"F0.wireOp",EDGE,"E21.filletArc");var subQ1=sQuery(id+"F0.wireOp",EDGE,"E7");var subQ2=sQuery(id+"F0.wireOp",EDGE,"E6");var subQ3=sQuery(id+"F0.wireOp",EDGE,"E5");var subQ4=sQuery(id+"F0.wireOp",EDGE,"E4");var subQ5=sQuery(id+"F0.wireOp",EDGE,"E22.filletArc");var subQ6=sQuery(id+"F0.wireOp",EDGE,"E1.bottom");var subQ7=sQuery(id+"F0.wireOp",EDGE,"E1.right");var subQ8=sQuery(id+"F0.wireOp",EDGE,"E1.top");var subQ9=sQuery(id+"F0.wireOp",EDGE,"E1.left");var subQ10=sQuery(id+"F0.wireOp",EDGE,"E23.filletArc");var subQ11=sQuery(id+"F0.wireOp",EDGE,"E24.filletArc");Q0=makeQuery(id+"F2.boolean.opBoolean","SPLIT",FACE,{"disambiguationData":[TD([makeQuery(id+"F1.opExtrude","SWEPT_FACE",FACE,{"disambiguationData":[OSD([subQ6])]})])],"derivedFrom":makeQuery(id+"F1.opExtrude","CAP_FACE",FACE,{"disambiguationData":[OSD([subQ6,subQ8,subQ9,subQ7,subQ4,subQ3,subQ2,subQ1,subQ0,subQ5,subQ10,subQ11])],"isStart":true})});}
            var sketch = newSketch(context, id + "F16", { "sketchPlane" : qUnion([Q0])});
            skLineSegment(sketch, "E79", {"start": v(0, 90) * mm, "end": v(0, 120) * mm, "construction": true});
            skPoint(sketch, "E79.endSnap0", {"position": v(0, 90) * mm});
            skCircle(sketch, "E80", {"center": v(0, 120) * mm, "radius": 6 * mm});
            skArc(sketch, "E81", {"start": v(15, 120) * mm, "mid": v(0, 135) * mm, "end": v(-15, 120) * mm});
            skLineSegment(sketch, "E82", {"start": v(-15, 120) * mm, "end": v(-15, 108) * mm});
            skLineSegment(sketch, "E83", {"start": v(15, 120) * mm, "end": v(15, 108) * mm});
            skLineSegment(sketch, "E84", {"start": v(15, 108) * mm, "end": v(33, 90) * mm});
            skLineSegment(sketch, "E85", {"start": v(-15, 108) * mm, "end": v(-33, 90) * mm});
            skLineSegment(sketch, "E86", {"start": v(0, -90) * mm, "end": v(0, -120) * mm, "construction": true});
            skCircle(sketch, "E87", {"center": v(0, -120) * mm, "radius": 6 * mm});
            skArc(sketch, "E88", {"start": v(-15, -120) * mm, "mid": v(0, -135) * mm, "end": v(15, -120) * mm});
            skLineSegment(sketch, "E89", {"start": v(-15, -120) * mm, "end": v(-15, -108) * mm});
            skLineSegment(sketch, "E90", {"start": v(15, -120) * mm, "end": v(15, -108) * mm});
            skLineSegment(sketch, "E91", {"start": v(-15, -108) * mm, "end": v(-33, -90) * mm});
            skLineSegment(sketch, "E92", {"start": v(15, -108) * mm, "end": v(33, -90) * mm});
            skSolve(sketch);
        }
        {
            var Q0;
            Q0=makeQuery(id+"F16.imprint","IMPRINT",FACE,{"disambiguationData":[TD([[makeQuery(id+"F16.imprint","IMPRINT",EDGE,{"derivedFrom":makeQuery(id+"F1.opExtrude","CAP_EDGE",EDGE,{"disambiguationData":[OSD([sQuery(id+"F0.wireOp",EDGE,"E1.left")])],"isStart":true})}),-1.0]])]});
            var Q1;
            Q1=makeQuery(id+"F16.imprint","IMPRINT",FACE,{"disambiguationData":[TD([[makeQuery(id+"F16.imprint","IMPRINT",EDGE,{"derivedFrom":sQuery(id+"F16.wireOp",EDGE,"E80")}),-1.0]])]});
            var Q2;
            Q2=makeQuery(id+"F16.imprint","IMPRINT",FACE,{"disambiguationData":[TD([[makeQuery(id+"F16.imprint","IMPRINT",EDGE,{"derivedFrom":sQuery(id+"F16.wireOp",EDGE,"E87")}),-1.0]])]});
            var Q3;
            Q3=makeQuery(id+"F2.opExtrude","CAP_FACE",FACE,{"disambiguationData":[OSD([sQuery(id+"F0.wireOp",EDGE,"E12"),sQuery(id+"F0.wireOp",EDGE,"E13"),sQuery(id+"F0.wireOp",EDGE,"E14"),sQuery(id+"F0.wireOp",EDGE,"E15"),sQuery(id+"F0.wireOp",EDGE,"E17.filletArc"),sQuery(id+"F0.wireOp",EDGE,"E18.filletArc"),sQuery(id+"F0.wireOp",EDGE,"E19.filletArc"),sQuery(id+"F0.wireOp",EDGE,"E20.filletArc"),sQuery(id+"F0.wireOp",EDGE,"E25.0"),sQuery(id+"F0.wireOp",EDGE,"E25.1"),sQuery(id+"F0.wireOp",EDGE,"E25.2"),sQuery(id+"F0.wireOp",EDGE,"E25.3"),sQuery(id+"F0.wireOp",EDGE,"E25.4"),sQuery(id+"F0.wireOp",EDGE,"E25.5"),sQuery(id+"F0.wireOp",EDGE,"E25.6"),sQuery(id+"F0.wireOp",EDGE,"E25.7")])],"isStart":false});
            extrude(context, id + "F17", {"entities" : qUnion([Q0, Q1, Q2]), "endBound" : BoundingType.UP_TO_SURFACE, "endBoundEntityFace" : qUnion([Q3]), "depth" : 25 * mm});
        }
    });
